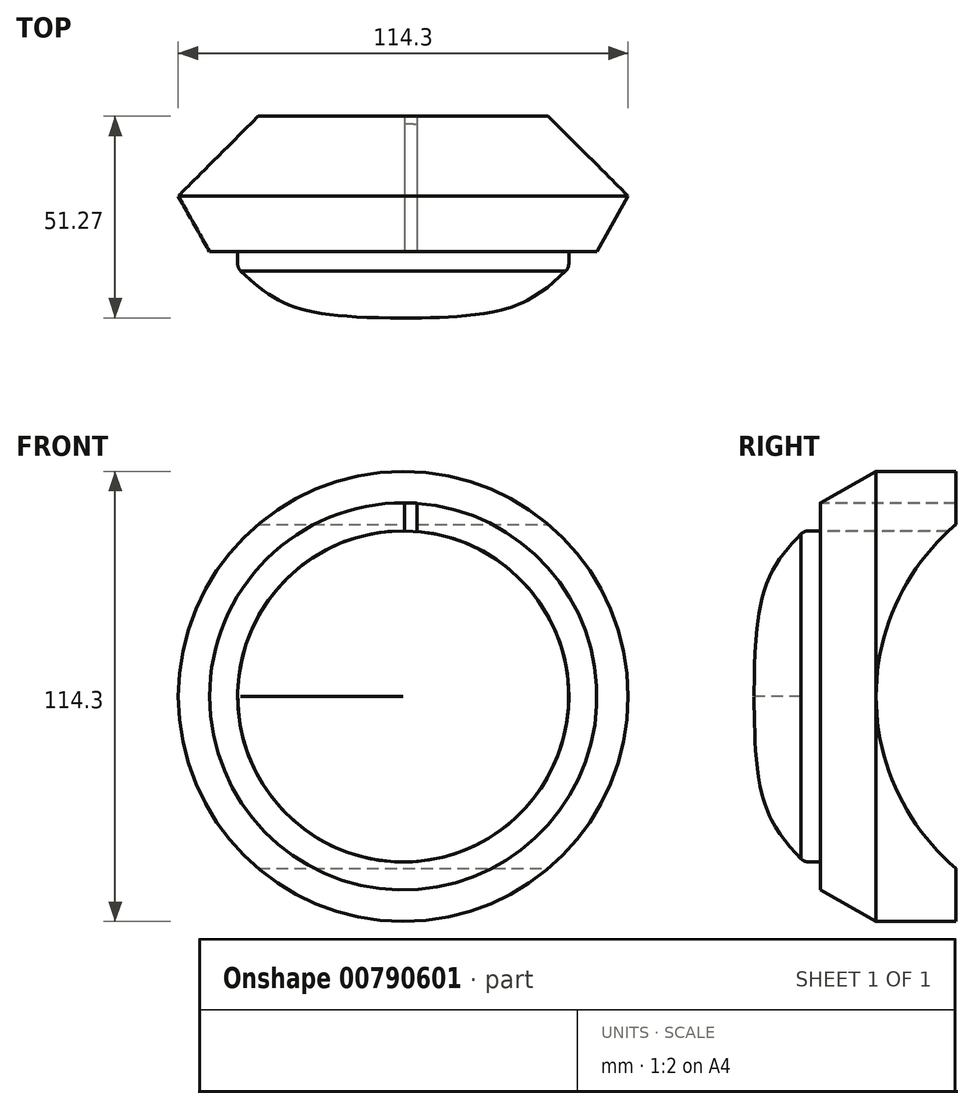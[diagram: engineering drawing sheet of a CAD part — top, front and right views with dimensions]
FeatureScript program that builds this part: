
annotation { "Feature Type Name" : "Feature", "Feature Type Description" : "" }
export const myFeature = defineFeature(function(context is Context, id is Id, definition is map)
    precondition{}
    {
        {
            var Q0;
            Q0=qCreatedBy(makeId("Top.planeOp"),FACE);
            var sketch = newSketch(context, id + "F0", { "sketchPlane" : qUnion([Q0])});
            skLineSegment(sketch, "E0", {"start": v(23.95, 66.81) * mm, "end": v(23.95, -21.29) * mm});
            skLineSegment(sketch, "E1", {"start": v(23.95, -4.46) * mm, "end": v(-25.24, -4.46) * mm});
            skLineSegment(sketch, "E2", {"start": v(23.95, -8.59) * mm, "end": v(-18.1, -8.59) * mm});
            skFitSpline(sketch, "E3", {"points": [v(-18.1, -8.59) * mm, v(23.95, -21.29) * mm], "startDerivative": vector(29.67, -29.15) * mm, "endDerivative": vector(79.63, 0) * mm});
            skLineSegment(sketch, "E4", {"start": v(-18.1, -8.59) * mm, "end": v(-18.1, -4.46) * mm});
            skLineSegment(sketch, "E5", {"start": v(-25.24, -4.46) * mm, "end": v(-33.2, 9.66) * mm});
            skLineSegment(sketch, "E6", {"start": v(-33.2, 9.66) * mm, "end": v(23.95, 9.66) * mm});
            skLineSegment(sketch, "E7", {"start": v(23.95, 9.66) * mm, "end": v(23.95, -4.46) * mm});
            skSolve(sketch);
        }
        {
            var Q0;
            {var subQ0=sQuery(id+"F0.wireOp",EDGE,"E5");Q0=makeQuery(id+"F0.imprint","IMPRINT",FACE,{"disambiguationData":[TD([[makeQuery(id+"F0.imprint","IMPRINT",EDGE,{"derivedFrom":subQ0}),-1.0]])]});}
            var Q1;
            {var subQ0=sQuery(id+"F0.wireOp",EDGE,"E2");Q1=makeQuery(id+"F0.imprint","IMPRINT",FACE,{"disambiguationData":[TD([[makeQuery(id+"F0.imprint","IMPRINT",EDGE,{"derivedFrom":subQ0}),-1.0]])]});}
            var Q2;
            {var subQ0=sQuery(id+"F0.wireOp",EDGE,"E2");Q2=makeQuery(id+"F0.imprint","IMPRINT",FACE,{"disambiguationData":[TD([[makeQuery(id+"F0.imprint","IMPRINT",EDGE,{"derivedFrom":subQ0}),1.0]])]});}
            var Q3;
            Q3=sQuery(id+"F0.wireOp",EDGE,"E0");
            revolve(context, id + "F1", {"surfaceOperationType" : NewSurfaceOperationType.NEW, "entities" : qUnion([Q0, Q1, Q2]), "axis" : qUnion([Q3]), "revolveType" : RevolveType.FULL});
        }
        {
            var Q0;
            Q0=makeQuery(id+"F1.opRevolve","SWEPT_FACE",FACE,{"disambiguationData":[OSD([sQuery(id+"F0.wireOp",EDGE,"E6")])]});
            var sketch = newSketch(context, id + "F2", { "sketchPlane" : qUnion([Q0])});
            skLineSegment(sketch, "E8", {"start": v(-23.95, 57.15) * mm, "end": v(-23.95, -57.15) * mm});
            skCircle(sketch, "E9", {"center": v(-23.95, 0) * mm, "radius": 57.15 * mm});
            skSolve(sketch);
        }
        {
            var Q0;
            {var subQ0=sQuery(id+"F2.wireOp",EDGE,"E8");Q0=makeQuery(id+"F2.imprint","IMPRINT",FACE,{"disambiguationData":[TD([[makeQuery(id+"F2.imprint","IMPRINT",EDGE,{"derivedFrom":subQ0}),1.0]])]});}
            var Q1;
            {var subQ0=sQuery(id+"F2.wireOp",EDGE,"E8");Q1=makeQuery(id+"F2.imprint","IMPRINT",FACE,{"disambiguationData":[TD([[makeQuery(id+"F2.imprint","IMPRINT",EDGE,{"derivedFrom":subQ0}),-1.0]])]});}
            extrude(context, id + "F3", {"entities" : qUnion([Q0, Q1]), "operationType" : NewBodyOperationType.ADD, "depth" : 20.32 * mm, "offsetDistance" : 25.4 * mm});
        }
        {
            var Q0;
            Q0=qCreatedBy(makeId("Right.planeOp"),FACE);
            var sketch = newSketch(context, id + "F4", { "sketchPlane" : qUnion([Q0])});
            skCircle(sketch, "E10", {"center": v(66.81, 0) * mm, "radius": 57.15 * mm});
            skLineSegment(sketch, "E11", {"start": v(66.81, 0) * mm, "end": v(9.66, 0) * mm});
            skSolve(sketch);
        }
        {
            var Q0;
            {var subQ0=sQuery(id+"F4.wireOp",EDGE,"E10");Q0=makeQuery(id+"F4.imprint","IMPRINT",FACE,{"disambiguationData":[TD([[makeQuery(id+"F4.imprint","IMPRINT",EDGE,{"disambiguationData":[TD([[makeQuery(id+"F4.imprint","IMPRINT",VERTEX,{"derivedFrom":subQ0}),-1.0]])],"derivedFrom":subQ0}),1.0]])]});}
            extrude(context, id + "F5", {"entities" : qUnion([Q0]), "operationType" : NewBodyOperationType.REMOVE, "oppositeDirection" : true, "depth" : 101.6 * mm, "offsetDistance" : 25.4 * mm});
        }
        {
            var Q0;
            {var subQ0=sQuery(id+"F4.wireOp",EDGE,"E10");Q0=makeQuery(id+"F4.imprint","IMPRINT",FACE,{"disambiguationData":[TD([[makeQuery(id+"F4.imprint","IMPRINT",EDGE,{"disambiguationData":[TD([[makeQuery(id+"F4.imprint","IMPRINT",VERTEX,{"derivedFrom":subQ0}),-1.0]])],"derivedFrom":subQ0}),1.0]])]});}
            extrude(context, id + "F6", {"entities" : qUnion([Q0]), "operationType" : NewBodyOperationType.REMOVE, "depth" : 152.4 * mm, "offsetDistance" : 25.4 * mm});
        }
        {
            var Q0;
            Q0=makeQuery(id+"F1.opRevolve","SWEPT_FACE",FACE,{"disambiguationData":[OSD([sQuery(id+"F0.wireOp",EDGE,"E1")])]});
            var sketch = newSketch(context, id + "F7", { "sketchPlane" : qUnion([Q0])});
            skLineSegment(sketch, "E12", {"start": v(24.24, 42.05) * mm, "end": v(24.24, 49.19) * mm});
            skLineSegment(sketch, "E13", {"start": v(27.4, 41.91) * mm, "end": v(27.4, 49.07) * mm});
            skArc(sketch, "E14", {"start": v(27.4, 49.07) * mm, "mid": v(25.82, 49.15) * mm, "end": v(24.24, 49.19) * mm});
            skArc(sketch, "E15", {"start": v(24.24, 42.05) * mm, "mid": v(22.07, -42.01) * mm, "end": v(27.4, 41.91) * mm});
            skSolve(sketch);
        }
        {
            var Q0;
            {var subQ0=sQuery(id+"F7.wireOp",EDGE,"E12");Q0=makeQuery(id+"F7.imprint","IMPRINT",FACE,{"disambiguationData":[TD([[makeQuery(id+"F7.imprint","IMPRINT",EDGE,{"derivedFrom":subQ0}),-1.0]])]});}
            extrude(context, id + "F8", {"entities" : qUnion([Q0]), "operationType" : NewBodyOperationType.REMOVE, "oppositeDirection" : true, "depth" : 50.8 * mm, "offsetDistance" : 25.4 * mm});
        }
        {
            var Q0;
            Q0=qCreatedBy(makeId("Top.planeOp"),FACE);
            var sketch = newSketch(context, id + "F9", { "sketchPlane" : qUnion([Q0])});
            skLineSegment(sketch, "E16", {"start": v(23.95, -26.22) * mm, "end": v(23.95, 49.05) * mm});
            skSolve(sketch);
        }
        {
            var Q0;
            Q0=makeQuery(id+"F1.opRevolve","SWEPT_EDGE",EDGE,{"disambiguationData":[OSD([sQuery(id+"F0.wireOp",EDGE,"E2"),sQuery(id+"F0.wireOp",EDGE,"E3"),sQuery(id+"F0.wireOp",EDGE,"E4")])]});
            fillet(context, id + "F10", {"entities" : qUnion([Q0]), "radius" : 2.54 * mm, "tangentPropagation" : true, "allowEdgeOverflow" : false});
        }
    });
